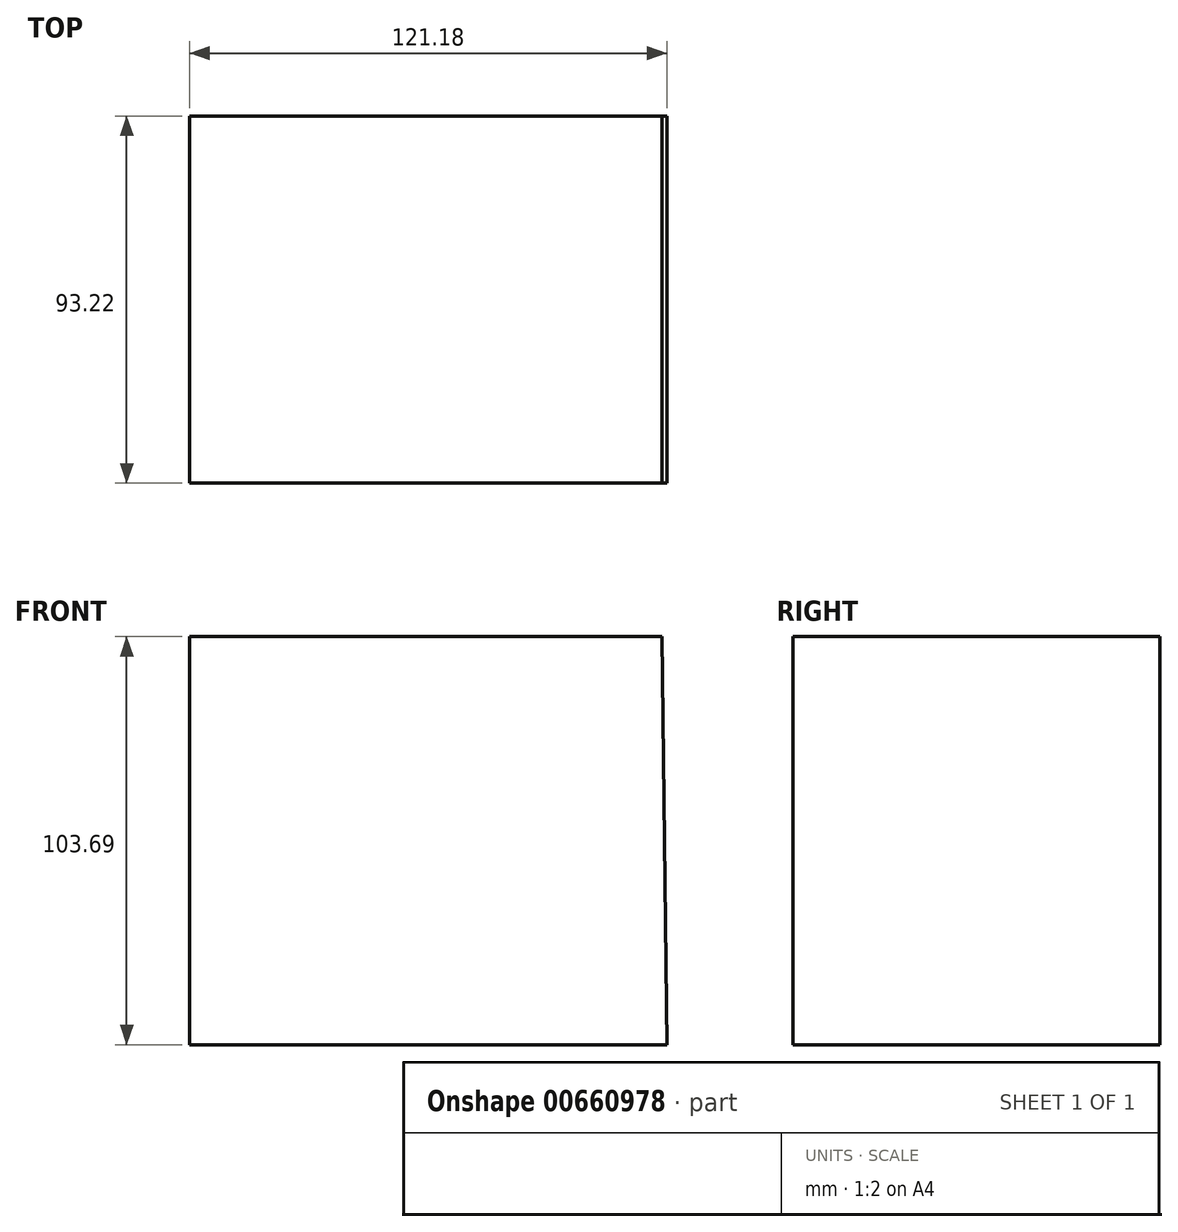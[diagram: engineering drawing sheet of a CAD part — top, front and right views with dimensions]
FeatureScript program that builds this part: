
annotation { "Feature Type Name" : "Feature", "Feature Type Description" : "" }
export const myFeature = defineFeature(function(context is Context, id is Id, definition is map)
    precondition{}
    {
        {
            var Q0;
            Q0=qCreatedBy(makeId("Front.planeOp"),FACE);
            var sketch = newSketch(context, id + "F0", { "sketchPlane" : qUnion([Q0])});
            skLineSegment(sketch, "E0", {"start": v(-56.02, 59.77) * mm, "end": v(-56.02, -43.92) * mm});
            skLineSegment(sketch, "E1", {"start": v(-56.02, -43.92) * mm, "end": v(65.16, -43.92) * mm});
            skLineSegment(sketch, "E2", {"start": v(-56.02, 59.77) * mm, "end": v(63.98, 59.77) * mm});
            skLineSegment(sketch, "E3", {"start": v(63.98, 59.77) * mm, "end": v(65.16, -43.92) * mm});
            skSolve(sketch);
        }
        {
            var Q0;
            Q0 = qSketchRegion(id + "F0", true);
            extrude(context, id + "F1", {"entities" : qUnion([Q0]), "depth" : 93.22 * mm, "offsetDistance" : 25.4 * mm});
        }
    });
